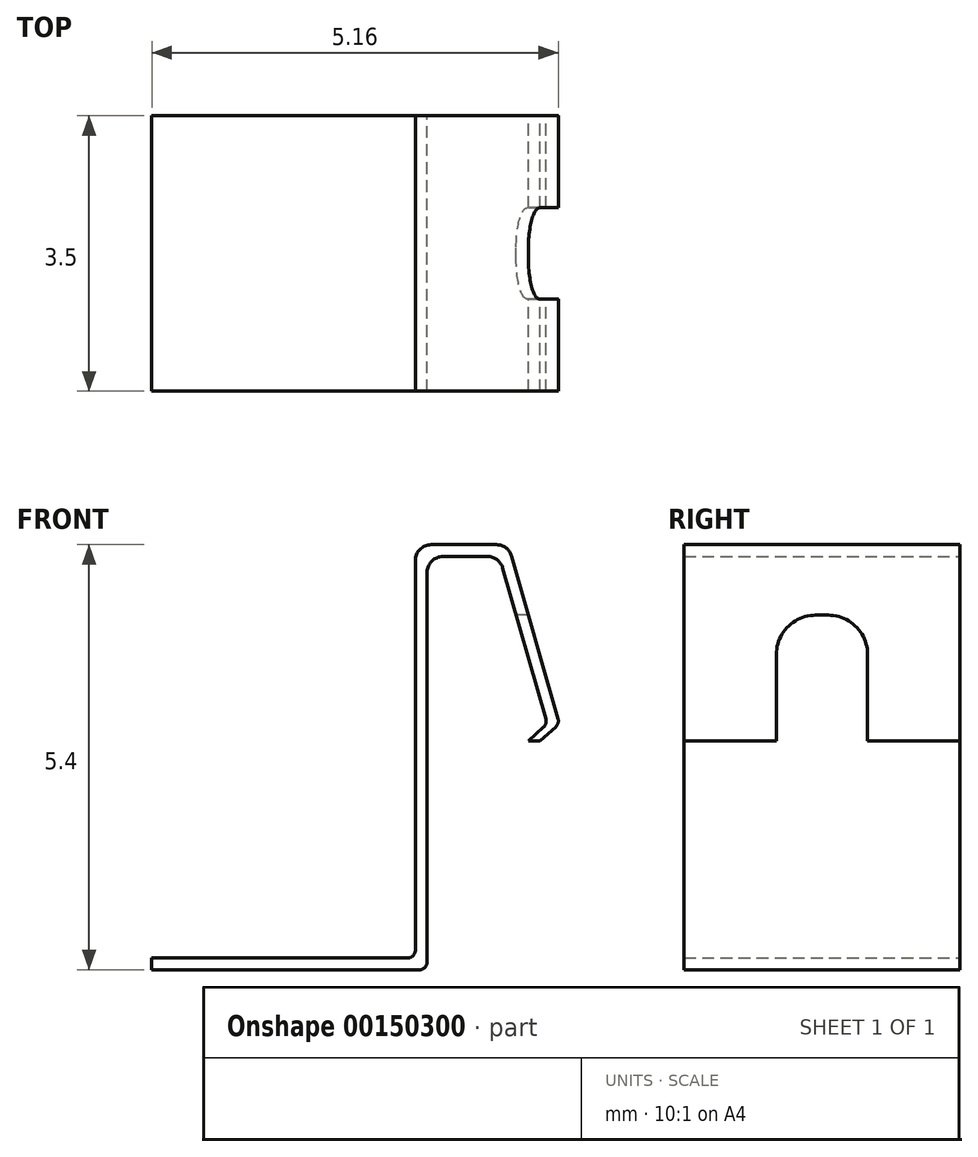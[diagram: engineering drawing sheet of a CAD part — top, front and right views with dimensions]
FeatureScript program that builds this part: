
annotation { "Feature Type Name" : "Feature", "Feature Type Description" : "" }
export const myFeature = defineFeature(function(context is Context, id is Id, definition is map)
    precondition{}
    {
        {
            var Q0;
            Q0=qCreatedBy(makeId("Front.planeOp"),FACE);
            var sketch = newSketch(context, id + "F0", { "sketchPlane" : qUnion([Q0])});
            skLineSegment(sketch, "E0.left", {"start": v(-2.65, 0.15) * mm, "end": v(-2.65, 0) * mm});
            skLineSegment(sketch, "E1", {"start": v(0.6, 0.15) * mm, "end": v(-2.65, 0.15) * mm});
            skLineSegment(sketch, "E2", {"start": v(-2.65, 0) * mm, "end": v(0.75, 0) * mm});
            skPoint(sketch, "E3.visualSharp", {"position": v(0.7, 0.15) * mm});
            skArc(sketch, "E3.filletArc", {"start": v(0.6, 0.15) * mm, "mid": v(0.67, 0.18) * mm, "end": v(0.7, 0.25) * mm});
            skPoint(sketch, "E4.visualSharp", {"position": v(0.85, 0) * mm});
            skArc(sketch, "E4.filletArc", {"start": v(0.75, 0) * mm, "mid": v(0.82, 0.03) * mm, "end": v(0.85, 0.1) * mm});
            skLineSegment(sketch, "E5.left", {"start": v(0.7, 5.2) * mm, "end": v(0.7, 2.91) * mm});
            skLineSegment(sketch, "E6", {"start": v(2.28, 2.91) * mm, "end": v(2.48, 3.09) * mm});
            skLineSegment(sketch, "E7", {"start": v(2.13, 2.91) * mm, "end": v(2.32, 3.08) * mm});
            skLineSegment(sketch, "E8", {"start": v(2.5, 3.19) * mm, "end": v(1.92, 5.25) * mm});
            skLineSegment(sketch, "E9", {"start": v(2.35, 3.19) * mm, "end": v(1.8, 5.1) * mm});
            skLineSegment(sketch, "E10", {"start": v(1.61, 5.25) * mm, "end": v(1.04, 5.25) * mm});
            skLineSegment(sketch, "E11", {"start": v(1.73, 5.4) * mm, "end": v(0.9, 5.4) * mm});
            skLineSegment(sketch, "E12", {"start": v(0.84, 5.05) * mm, "end": v(0.85, 0.1) * mm});
            skLineSegment(sketch, "E13", {"start": v(2.28, 2.91) * mm, "end": v(2.13, 2.91) * mm});
            skPoint(sketch, "E14.visualSharp", {"position": v(2.37, 3.12) * mm});
            skArc(sketch, "E14.filletArc", {"start": v(2.32, 3.08) * mm, "mid": v(2.35, 3.13) * mm, "end": v(2.35, 3.19) * mm});
            skPoint(sketch, "E15.visualSharp", {"position": v(2.53, 3.13) * mm});
            skArc(sketch, "E15.filletArc", {"start": v(2.48, 3.09) * mm, "mid": v(2.5, 3.13) * mm, "end": v(2.5, 3.19) * mm});
            skPoint(sketch, "E16.visualSharp", {"position": v(1.88, 5.4) * mm});
            skArc(sketch, "E16.filletArc", {"start": v(1.92, 5.25) * mm, "mid": v(1.85, 5.36) * mm, "end": v(1.73, 5.4) * mm});
            skPoint(sketch, "E17.visualSharp", {"position": v(1.76, 5.25) * mm});
            skArc(sketch, "E17.filletArc", {"start": v(1.8, 5.1) * mm, "mid": v(1.73, 5.2) * mm, "end": v(1.61, 5.25) * mm});
            skPoint(sketch, "E18.visualSharp", {"position": v(0.84, 5.25) * mm});
            skArc(sketch, "E18.filletArc", {"start": v(1.04, 5.25) * mm, "mid": v(0.9, 5.2) * mm, "end": v(0.85, 5.05) * mm});
            skPoint(sketch, "E19.visualSharp", {"position": v(0.7, 5.4) * mm});
            skArc(sketch, "E19.filletArc", {"start": v(0.9, 5.4) * mm, "mid": v(0.75, 5.34) * mm, "end": v(0.7, 5.2) * mm});
            skLineSegment(sketch, "E20", {"start": v(0.7, 0.25) * mm, "end": v(0.7, 2.91) * mm});
            skSolve(sketch);
        }
        {
            var Q0;
            Q0 = qSketchRegion(id + "F0", true);
            extrude(context, id + "F1", {"entities" : qUnion([Q0]), "depth" : 1.75 * mm, "hasSecondDirection" : true, "secondDirectionOppositeDirection" : true, "secondDirectionDepth" : 1.75 * mm});
        }
        {
            var Q0;
            Q0=makeQuery(id+"F1.opExtrude","SWEPT_FACE",FACE,{"disambiguationData":[OSD([sQuery(id+"F0.wireOp",EDGE,"E12")])]});
            var sketch = newSketch(context, id + "F2", { "sketchPlane" : qUnion([Q0])});
            skLineSegment(sketch, "E21.bottom", {"start": v(-0.58, 2.61) * mm, "end": v(0.58, 2.61) * mm});
            skLineSegment(sketch, "E21.top", {"start": v(-0.08, 4.5) * mm, "end": v(0.08, 4.5) * mm});
            skLineSegment(sketch, "E21.left", {"start": v(-0.58, 2.61) * mm, "end": v(-0.58, 4) * mm});
            skLineSegment(sketch, "E21.right", {"start": v(0.58, 2.61) * mm, "end": v(0.58, 4) * mm});
            skPoint(sketch, "E22.visualSharp", {"position": v(-0.58, 4.5) * mm});
            skArc(sketch, "E22.filletArc", {"start": v(-0.08, 4.5) * mm, "mid": v(-0.43, 4.36) * mm, "end": v(-0.58, 4) * mm});
            skPoint(sketch, "E23.visualSharp", {"position": v(0.58, 4.5) * mm});
            skArc(sketch, "E23.filletArc", {"start": v(0.58, 4) * mm, "mid": v(0.43, 4.36) * mm, "end": v(0.08, 4.5) * mm});
            skSolve(sketch);
        }
        {
            var Q0;
            Q0 = qSketchRegion(id + "F2", true);
            extrude(context, id + "F3", {"entities" : qUnion([Q0]), "operationType" : NewBodyOperationType.REMOVE, "depth" : 25 * mm});
        }
    });
